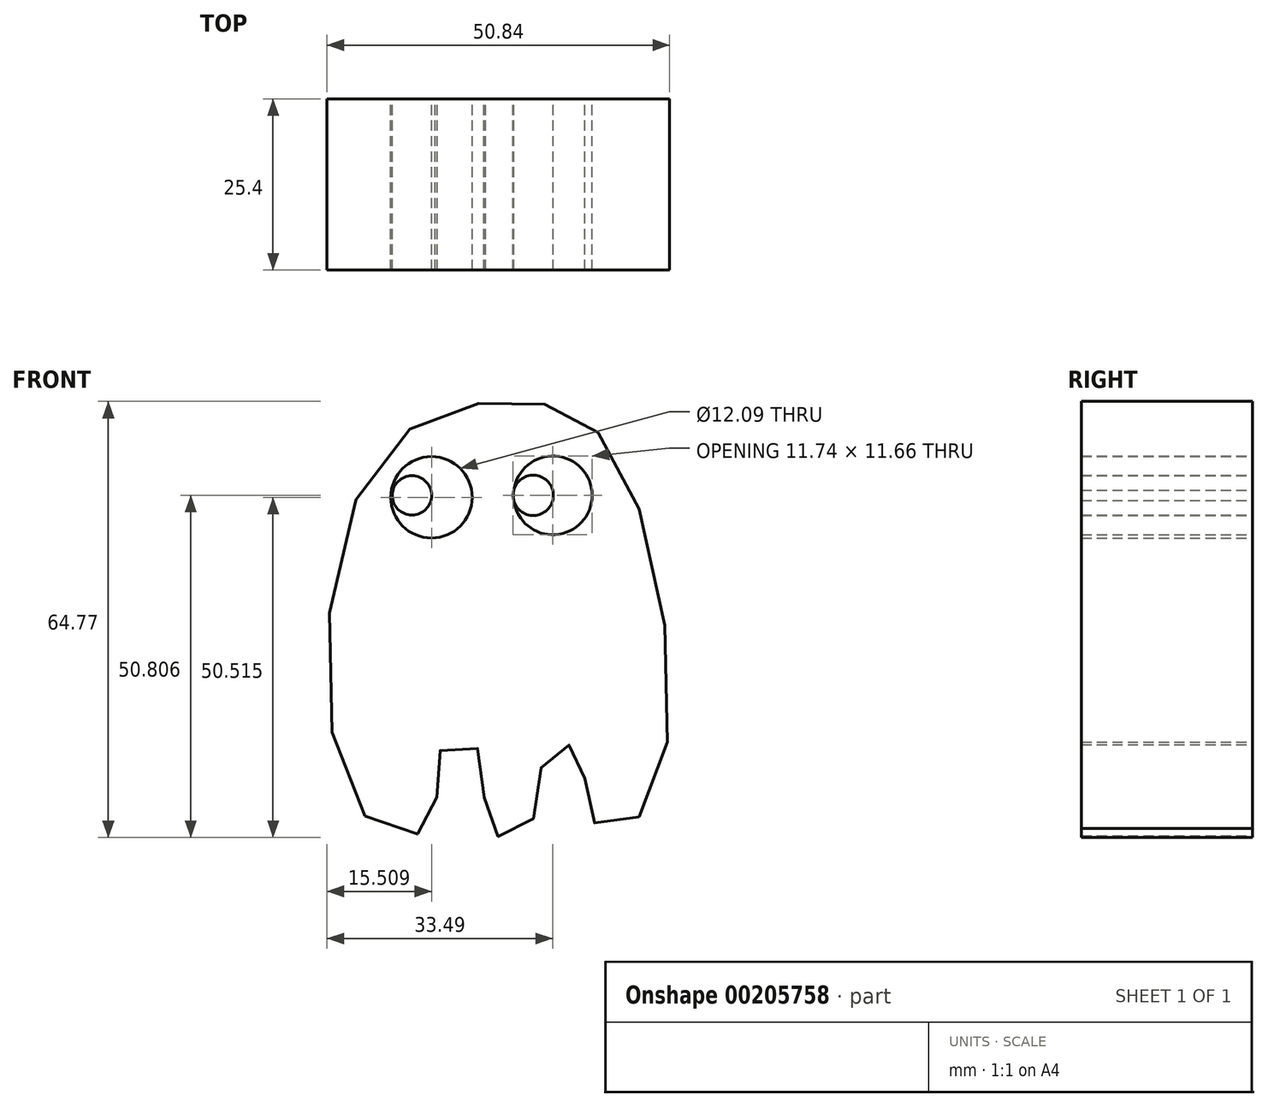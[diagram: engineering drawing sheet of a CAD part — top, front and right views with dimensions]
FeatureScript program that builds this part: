
annotation { "Feature Type Name" : "Feature", "Feature Type Description" : "" }
export const myFeature = defineFeature(function(context is Context, id is Id, definition is map)
    precondition{}
    {
        {
            var Q0;
            Q0=qCreatedBy(makeId("Front.planeOp"),FACE);
            var sketch = newSketch(context, id + "F0", { "sketchPlane" : qUnion([Q0])});
            skFitSpline(sketch, "E0", {"points": [v(-38.04, -12.34) * mm, v(-37.46, 38.48) * mm, v(-15.4, 49.23) * mm, v(0, 39.64) * mm, v(3.78, -11.18) * mm, v(-4.65, -12.63) * mm, v(-6.1, -2.76) * mm, v(-11.04, -3.05) * mm, v(-13.65, -13.8) * mm, v(-19.75, -14.38) * mm, v(-20.91, -2.76) * mm, v(-27, -2.76) * mm, v(-27.88, -13.21) * mm, v(-38.04, -12.34) * mm]});
            skCircle(sketch, "E1", {"center": v(-28.17, 35) * mm, "radius": 6.04 * mm});
            skCircle(sketch, "E2", {"center": v(-10.16, 35.29) * mm, "radius": 5.84 * mm});
            skPoint(sketch, "E3.orphan", {"position": v(-16, 35) * mm});
            skCircle(sketch, "E4", {"center": v(-31.07, 35.29) * mm, "radius": 2.92 * mm});
            skCircle(sketch, "E5", {"center": v(-13.07, 35.29) * mm, "radius": 3 * mm});
            skSolve(sketch);
        }
        {
            var Q0;
            Q0=makeQuery(id+"F0.imprint","IMPRINT",FACE,{"disambiguationData":[TD([[makeQuery(id+"F0.imprint","IMPRINT",EDGE,{"derivedFrom":sQuery(id+"F0.wireOp",EDGE,"E0")}),-1.0]])]});
            var Q1;
            Q1=makeQuery(id+"F0.imprint","IMPRINT",FACE,{"disambiguationData":[TD([[makeQuery(id+"F0.imprint","IMPRINT",EDGE,{"derivedFrom":sQuery(id+"F0.wireOp",EDGE,"E4")}),1.0]])]});
            var Q2;
            {var subQ0=sQuery(id+"F0.wireOp",EDGE,"E5");var subQ1=sQuery(id+"F0.wireOp",EDGE,"E2");var subQ2=makeQuery(id+"F0.imprint","INTERSECT",VERTEX,{"disambiguationData":[OD(0.0)],"derivedFrom":[subQ1,subQ0]});Q2=makeQuery(id+"F0.imprint","IMPRINT",FACE,{"disambiguationData":[TD([[makeQuery(id+"F0.imprint","IMPRINT",EDGE,{"disambiguationData":[TD([[subQ2,1.0]])],"derivedFrom":subQ1}),1.0]])]});}
            extrude(context, id + "F1", {"entities" : qUnion([Q0, Q1, Q2]), "depth" : 25.4 * mm});
        }
    });
